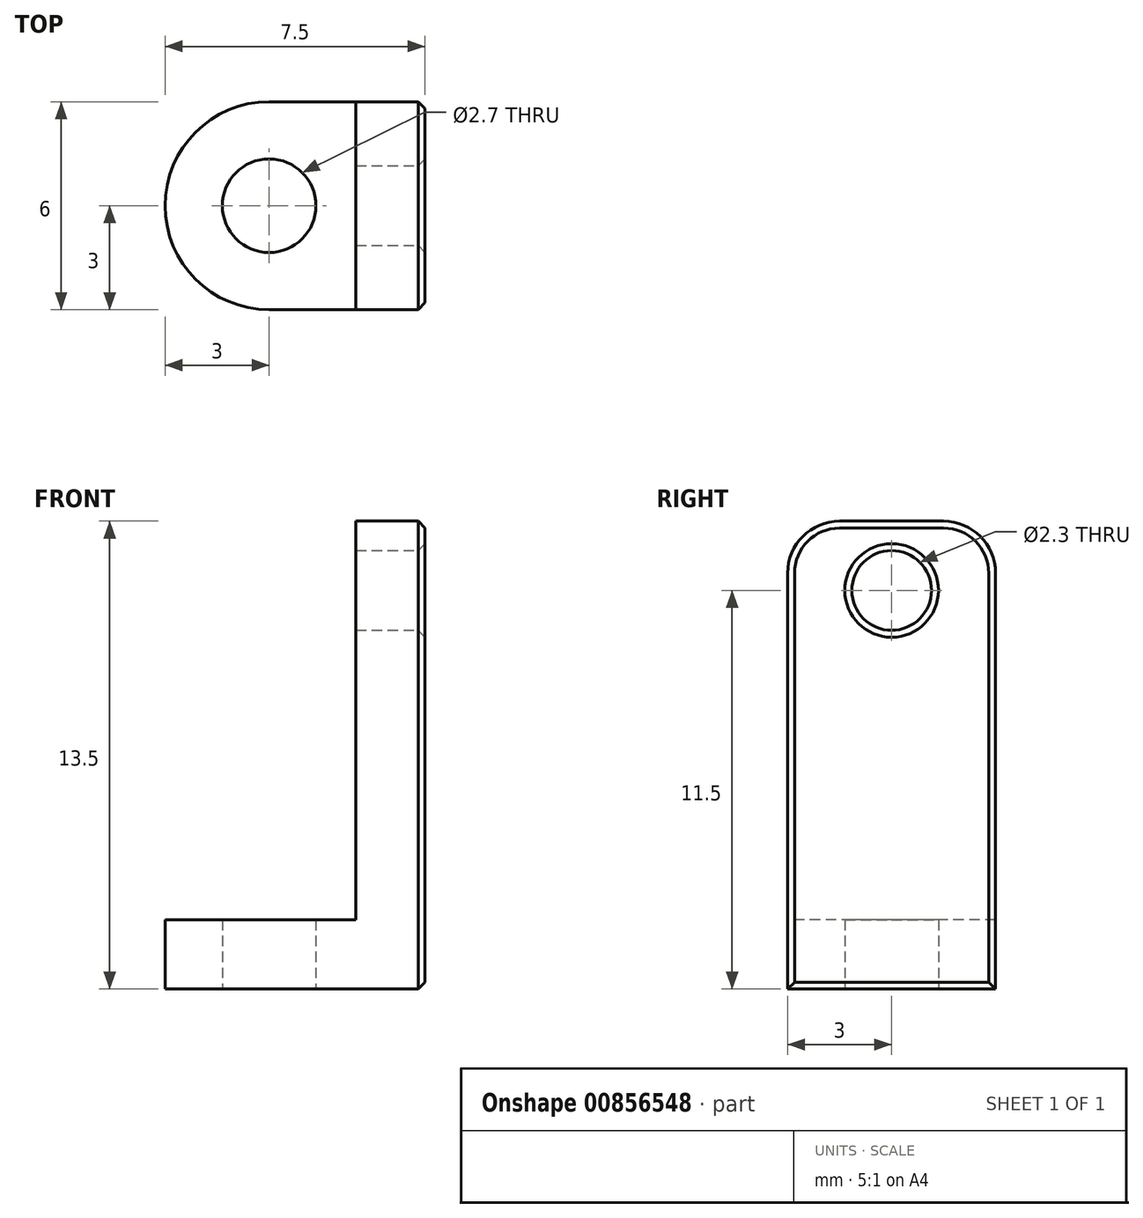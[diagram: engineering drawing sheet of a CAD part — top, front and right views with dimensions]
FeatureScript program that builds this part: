
annotation { "Feature Type Name" : "Feature", "Feature Type Description" : "" }
export const myFeature = defineFeature(function(context is Context, id is Id, definition is map)
    precondition{}
    {
        {
            var Q0;
            Q0=qCreatedBy(makeId("Top.planeOp"),FACE);
            var sketch = newSketch(context, id + "F0", { "sketchPlane" : qUnion([Q0])});
            skCircle(sketch, "E0", {"center": v(-14, 0) * mm, "radius": 1.25 * mm, "construction": true});
            skCircle(sketch, "E1.0", {"center": v(-14, 0) * mm, "radius": 1.35 * mm});
            skCircle(sketch, "E2.MirrorC", {"center": v(14, 0) * mm, "radius": 1.35 * mm, "construction": true});
            skLineSegment(sketch, "E3", {"start": v(-14, 0) * mm, "end": v(14, 0) * mm, "construction": true});
            skLineSegment(sketch, "E4", {"start": v(-9.5, 3) * mm, "end": v(-9.5, -3) * mm});
            skLineSegment(sketch, "E5", {"start": v(-9.5, 3) * mm, "end": v(-14, 3) * mm});
            skLineSegment(sketch, "E6", {"start": v(-9.5, -3) * mm, "end": v(-14, -3) * mm});
            skArc(sketch, "E7", {"start": v(-14, 3) * mm, "mid": v(-17, 0) * mm, "end": v(-14, -3) * mm});
            skLineSegment(sketch, "E8.MirrorCS", {"start": v(9.5, 3) * mm, "end": v(9.5, -3) * mm, "construction": true});
            skLineSegment(sketch, "E9.MirrorCS", {"start": v(9.5, 3) * mm, "end": v(14, 3) * mm, "construction": true});
            skArc(sketch, "E10.MirrorCS", {"start": v(14, 3) * mm, "mid": v(17, 0) * mm, "end": v(14, -3) * mm, "construction": true});
            skLineSegment(sketch, "E11.MirrorCS", {"start": v(9.5, -3) * mm, "end": v(14, -3) * mm, "construction": true});
            skSolve(sketch);
        }
        {
            var Q0;
            Q0=qCreatedBy(makeId("Top.planeOp"),FACE);
            var sketch = newSketch(context, id + "F1", { "sketchPlane" : qUnion([Q0])});
            skLineSegment(sketch, "E12.0", {"start": v(-9.5, 3) * mm, "end": v(-9.5, -3) * mm});
            skLineSegment(sketch, "E13", {"start": v(-9.5, 3) * mm, "end": v(-11.5, 3) * mm});
            skLineSegment(sketch, "E14", {"start": v(-11.5, 3) * mm, "end": v(-11.5, -3) * mm});
            skLineSegment(sketch, "E15", {"start": v(-11.5, -3) * mm, "end": v(-9.5, -3) * mm});
            skSolve(sketch);
        }
        {
            var Q0;
            Q0=qCreatedBy(makeId("Front.planeOp"),FACE);
            var sketch = newSketch(context, id + "F2", { "sketchPlane" : qUnion([Q0])});
            skLineSegment(sketch, "E16", {"start": v(0, -2) * mm, "end": v(0, 0) * mm});
            skLineSegment(sketch, "E17", {"start": v(0, 0) * mm, "end": v(0, 11.5) * mm});
            skPoint(sketch, "E18", {"position": v(0, 9.5) * mm});
            skSolve(sketch);
        }
        {
            var Q0;
            Q0 = qSketchRegion(id + "F0", true);
            var Q1;
            Q1=sQuery(id+"F2.wireOp",EDGE,"E16");
            sweep(context, id + "F3", {"profiles" : qUnion([Q0]), "path" : qUnion([Q1])});
        }
        {
            var Q0;
            Q0 = qSketchRegion(id + "F1", true);
            var Q1;
            Q1=sQuery(id+"F2.wireOp",EDGE,"E17");
            sweep(context, id + "F4", {"operationType" : NewBodyOperationType.ADD, "profiles" : qUnion([Q0]), "path" : qUnion([Q1])});
        }
        {
            var Q0;
            Q0=qCreatedBy(makeId("Right.planeOp"),FACE);
            var sketch = newSketch(context, id + "F5", { "sketchPlane" : qUnion([Q0])});
            skPoint(sketch, "E19.0", {"position": v(0, 9.5) * mm});
            skCircle(sketch, "E20", {"center": v(0, 9.5) * mm, "radius": 1 * mm, "construction": true});
            skCircle(sketch, "E21.0", {"center": v(0, 9.5) * mm, "radius": 1.15 * mm});
            skSolve(sketch);
        }
        {
            var Q0;
            Q0=makeQuery(id+"F5.imprint","IMPRINT",FACE,{"disambiguationData":[TD([[makeQuery(id+"F5.imprint","IMPRINT",EDGE,{"derivedFrom":sQuery(id+"F5.wireOp",EDGE,"E21.0")}),1.0]])]});
            extrude(context, id + "F6", {"entities" : qUnion([Q0]), "operationType" : NewBodyOperationType.REMOVE, "endBound" : BoundingType.THROUGH_ALL, "oppositeDirection" : true, "depth" : 25 * mm, "offsetDistance" : 25 * mm});
        }
        {
            var Q0;
            Q0=makeQuery(id+"F4.opSweep","CAP_EDGE",EDGE,{"disambiguationData":[OSD([sQuery(id+"F1.wireOp",EDGE,"E13"),sQuery(id+"F2.wireOp",VERTEX,"E17.end")])],"isStart":false});
            var Q1;
            Q1=makeQuery(id+"F4.opSweep","CAP_EDGE",EDGE,{"disambiguationData":[OSD([sQuery(id+"F1.wireOp",EDGE,"E15"),sQuery(id+"F2.wireOp",VERTEX,"E17.end")])],"isStart":false});
            fillet(context, id + "F7", {"entities" : qUnion([Q0, Q1]), "radius" : 1.5 * mm, "allowEdgeOverflow" : false});
        }
        {
            var Q0;
            Q0=makeQuery(id+"F4.boolean.opBoolean","MERGE",FACE,{"derivedFrom":[makeQuery(id+"F3.opSweep","SWEPT_FACE",FACE,{"disambiguationData":[OSD([sQuery(id+"F0.wireOp",EDGE,"E4"),sQuery(id+"F2.wireOp",EDGE,"E16")])]}),makeQuery(id+"F4.opSweep","SWEPT_FACE",FACE,{"disambiguationData":[OSD([sQuery(id+"F1.wireOp",EDGE,"E12.0"),sQuery(id+"F2.wireOp",EDGE,"E17")])]})]});
            chamfer(context, id + "F8", {"entities" : qUnion([Q0]), "width" : 0.2 * mm});
        }
    });
